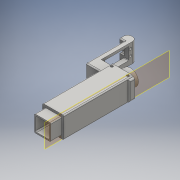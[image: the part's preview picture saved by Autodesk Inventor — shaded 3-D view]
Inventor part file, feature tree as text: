
AUTODESK INVENTOR PART (.ipt)
format: ipt  version: 2016 (Build 200138000, 138)  size: 433,664 bytes
history: native  units: mm
features: extrude x20, sketch x16, fillet x7, other x2, projected_geometry x2, mirror x1
ambient origin geometry x8: Origin, YZ Plane, XZ Plane, XY Plane, X Axis, Y Axis, Z Axis, Center Point
bodies: Body1 (feature_tree)
feature tree (48):
  other  "ソリッド1"
  extrude  "押し出し1"  Depth=31.0mm
  fillet  "フィレット1"  Radius=31.0mm
  extrude  "押し出し2"  Depth=20.0mm TaperAngle=0.0deg
  fillet  "フィレット2"  Radius=2.0mm
  extrude  "押し出し3"  Depth=4.5mm
  extrude  "押し出し5"  Depth=4.5mm
  extrude  "押し出し6"  Depth=4.5mm
  extrude  "押し出し7"  Depth=4.5mm
  extrude  "押し出し8"  Depth=30.0mm TaperAngle=0.0deg
  extrude  "押し出し9"  Depth=2.0mm
  extrude  "押し出し10"  Depth=2.0mm
  extrude  "押し出し11"  Depth=2.5mm
  sketch  "スケッチ11"
  extrude  "押し出し12"  Depth=2.5mm
  extrude  "押し出し13"  Depth=2.5mm
  extrude  "押し出し14"  Depth=2.5mm
  extrude  "押し出し15"  Depth=30.0mm TaperAngle=0.0deg
  extrude  "押し出し25"  Depth=2.0mm
  other  "作業平面1"
  extrude  "押し出し29"  Depth=3.0mm
  extrude  "押し出し30"  Depth=3.0mm
  fillet  "フィレット6"  Radius=3.0mm
  extrude  "押し出し31"  Depth=3.0mm
  extrude  "押し出し33"  Depth=90.0mm TaperAngle=0.0deg
  extrude  "押し出し34"  Depth=10.0mm TaperAngle=0.0deg
  fillet  "フィレット8"  Radius=30.0mm
  fillet  "フィレット9"  Radius=15.0mm
  fillet  "フィレット10"  Radius=3.0mm
  fillet  "フィレット11"  Radius=30.0mm
  mirror  "ミラー1"
  sketch  "スケッチ1"
  sketch  "スケッチ2"
  sketch  "スケッチ3"
  sketch  "スケッチ5"
  sketch  "スケッチ6"
  sketch  "スケッチ7"
  sketch  "スケッチ8"
  sketch  "スケッチ9"
  sketch  "スケッチ10"
  sketch  "スケッチ21"
  sketch  "スケッチ24"
  sketch  "スケッチ25"
  sketch  "スケッチ26"
  projected_geometry  "投影ループ1"
  sketch  "スケッチ28"
  sketch  "スケッチ29"
  projected_geometry  "投影ループ3"
